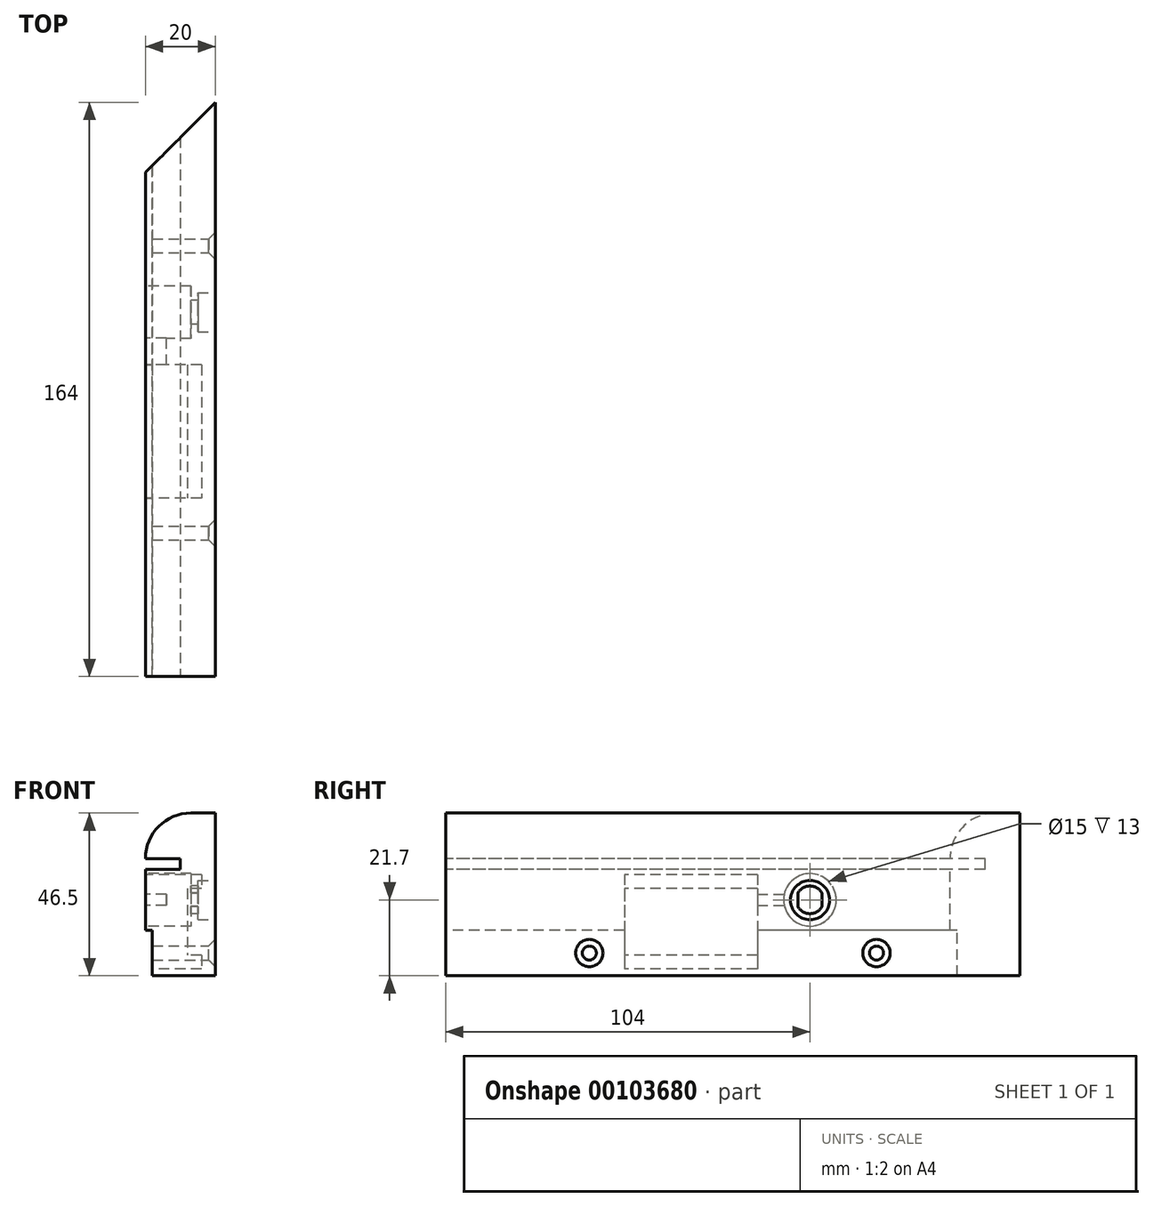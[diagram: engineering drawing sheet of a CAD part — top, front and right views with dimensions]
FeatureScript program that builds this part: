
annotation { "Feature Type Name" : "Feature", "Feature Type Description" : "" }
export const myFeature = defineFeature(function(context is Context, id is Id, definition is map)
    precondition{}
    {
        {
            var Q0;
            Q0=qCreatedBy(makeId("Front.planeOp"),FACE);
            var sketch = newSketch(context, id + "F0", { "sketchPlane" : qUnion([Q0])});
            skLineSegment(sketch, "E0.bottom", {"start": v(10, 23.25) * mm, "end": v(-10, 23.25) * mm});
            skLineSegment(sketch, "E0.top", {"start": v(10, -23.25) * mm, "end": v(-10, -23.25) * mm});
            skLineSegment(sketch, "E0.left", {"start": v(10, 23.25) * mm, "end": v(10, -23.25) * mm});
            skLineSegment(sketch, "E0.right", {"start": v(-10, 23.25) * mm, "end": v(-10, -23.25) * mm});
            skPoint(sketch, "E0.middle", {"position": v(0, 0) * mm});
            skSolve(sketch);
        }
        {
            var Q0;
            Q0=makeQuery(id+"F0.imprint","IMPRINT",FACE,{"disambiguationData":[TD([[makeQuery(id+"F0.imprint","IMPRINT",EDGE,{"derivedFrom":sQuery(id+"F0.wireOp",EDGE,"E0.bottom")}),1.0]])]});
            extrude(context, id + "F1", {"entities" : qUnion([Q0]), "depth" : 164 * mm});
        }
        {
            var Q0;
            Q0=makeQuery(id+"F1.opExtrude","SWEPT_FACE",FACE,{"disambiguationData":[OSD([sQuery(id+"F0.wireOp",EDGE,"E0.right")])]});
            var sketch = newSketch(context, id + "F2", { "sketchPlane" : qUnion([Q0])});
            skLineSegment(sketch, "E1.bottom", {"start": v(0, 10.25) * mm, "end": v(164, 10.25) * mm});
            skLineSegment(sketch, "E1.top", {"start": v(0, 7.15) * mm, "end": v(164, 7.15) * mm});
            skLineSegment(sketch, "E1.left", {"start": v(0, 10.25) * mm, "end": v(0, 7.15) * mm});
            skLineSegment(sketch, "E1.right", {"start": v(164, 10.25) * mm, "end": v(164, 7.15) * mm});
            skLineSegment(sketch, "E2.bottom", {"start": v(0, -23.25) * mm, "end": v(164, -23.25) * mm});
            skLineSegment(sketch, "E2.top", {"start": v(0, -10.25) * mm, "end": v(164, -10.25) * mm});
            skLineSegment(sketch, "E2.left", {"start": v(0, -23.25) * mm, "end": v(0, -10.25) * mm});
            skLineSegment(sketch, "E2.right", {"start": v(164, -23.25) * mm, "end": v(164, -10.25) * mm});
            skSolve(sketch);
        }
        {
            var Q0;
            Q0=makeQuery(id+"F2.imprint","IMPRINT",FACE,{"disambiguationData":[TD([[makeQuery(id+"F2.imprint","IMPRINT",EDGE,{"derivedFrom":sQuery(id+"F2.wireOp",EDGE,"E1.bottom")}),-1.0]])]});
            extrude(context, id + "F3", {"entities" : qUnion([Q0]), "operationType" : NewBodyOperationType.REMOVE, "oppositeDirection" : true, "depth" : 10 * mm});
        }
        {
            var Q0;
            {var subQ0=sQuery(id+"F0.wireOp",EDGE,"E0.right");var subQ2=sQuery(id+"F0.wireOp",EDGE,"E0.top");Q0=makeQuery(id+"F3.boolean.opBoolean","SPLIT",FACE,{"disambiguationData":[TD([makeQuery(id+"F1.opExtrude","SWEPT_FACE",FACE,{"disambiguationData":[OSD([subQ2])]})])],"derivedFrom":makeQuery(id+"F1.opExtrude","SWEPT_FACE",FACE,{"disambiguationData":[OSD([subQ0])]})});}
            var sketch = newSketch(context, id + "F4", { "sketchPlane" : qUnion([Q0])});
            skLineSegment(sketch, "E3.bottom", {"start": v(0, -23.25) * mm, "end": v(164, -23.25) * mm});
            skLineSegment(sketch, "E3.top", {"start": v(0, -10.25) * mm, "end": v(164, -10.25) * mm});
            skLineSegment(sketch, "E3.left", {"start": v(0, -23.25) * mm, "end": v(0, -10.25) * mm});
            skLineSegment(sketch, "E3.right", {"start": v(164, -23.25) * mm, "end": v(164, -10.25) * mm});
            skSolve(sketch);
        }
        {
            var Q0;
            Q0=makeQuery(id+"F4.imprint","IMPRINT",FACE,{"disambiguationData":[TD([[makeQuery(id+"F4.imprint","IMPRINT",EDGE,{"derivedFrom":sQuery(id+"F4.wireOp",EDGE,"E3.bottom")}),-1.0]])]});
            extrude(context, id + "F5", {"entities" : qUnion([Q0]), "operationType" : NewBodyOperationType.REMOVE, "oppositeDirection" : true, "depth" : 2 * mm});
        }
        {
            var Q0;
            Q0=makeQuery(id+"F1.opExtrude","SWEPT_FACE",FACE,{"disambiguationData":[OSD([sQuery(id+"F0.wireOp",EDGE,"E0.bottom")])]});
            var sketch = newSketch(context, id + "F6", { "sketchPlane" : qUnion([Q0])});
            skLineSegment(sketch, "E4.bottom", {"start": v(10, 0) * mm, "end": v(-10, 0) * mm, "construction": true});
            skLineSegment(sketch, "E4.top", {"start": v(10, -20) * mm, "end": v(-10, -20) * mm, "construction": true});
            skLineSegment(sketch, "E4.left", {"start": v(10, 0) * mm, "end": v(10, -20) * mm, "construction": true});
            skLineSegment(sketch, "E4.right", {"start": v(-10, 0) * mm, "end": v(-10, -20) * mm, "construction": true});
            skLineSegment(sketch, "E5", {"start": v(-10, -20) * mm, "end": v(10, 0) * mm});
            skLineSegment(sketch, "E6", {"start": v(-10, -20) * mm, "end": v(-10, 0) * mm});
            skLineSegment(sketch, "E7", {"start": v(-10, 0) * mm, "end": v(10, 0) * mm});
            skSolve(sketch);
        }
        {
            var Q0;
            Q0=makeQuery(id+"F6.imprint","IMPRINT",FACE,{"disambiguationData":[TD([[makeQuery(id+"F6.imprint","IMPRINT",EDGE,{"derivedFrom":sQuery(id+"F6.wireOp",EDGE,"E5")}),1.0]])]});
            var Q1;
            Q1=makeQuery(id+"F1.opExtrude","SWEPT_FACE",FACE,{"disambiguationData":[OSD([sQuery(id+"F0.wireOp",EDGE,"E0.top")])]});
            extrude(context, id + "F7", {"entities" : qUnion([Q0]), "operationType" : NewBodyOperationType.REMOVE, "endBound" : BoundingType.UP_TO_SURFACE, "oppositeDirection" : true, "endBoundEntityFace" : qUnion([Q1]), "depth" : 25 * mm});
        }
        {
            var Q0;
            Q0=makeQuery(id+"F1.opExtrude","SWEPT_EDGE",EDGE,{"disambiguationData":[OSD([sQuery(id+"F0.wireOp",EDGE,"E0.bottom"),sQuery(id+"F0.wireOp",EDGE,"E0.right")])]});
            fillet(context, id + "F8", {"entities" : qUnion([Q0]), "radius" : 13 * mm, "tangentPropagation" : true, "allowEdgeOverflow" : false});
        }
        {
            var Q0;
            Q0=makeQuery(id+"F1.opExtrude","SWEPT_FACE",FACE,{"disambiguationData":[OSD([sQuery(id+"F0.wireOp",EDGE,"E0.left")])]});
            var sketch = newSketch(context, id + "F9", { "sketchPlane" : qUnion([Q0])});
            skLineSegment(sketch, "E8", {"start": v(-82, 23.25) * mm, "end": v(-82, -23.25) * mm, "construction": true});
            skLineSegment(sketch, "E9", {"start": v(-164, -16.75) * mm, "end": v(-82, -16.75) * mm, "construction": true});
            skLineSegment(sketch, "E10", {"start": v(-82, -16.75) * mm, "end": v(0, -16.75) * mm, "construction": true});
            skPoint(sketch, "E11", {"position": v(-123, -16.75) * mm});
            skPoint(sketch, "E12", {"position": v(-41, -16.75) * mm});
            skSolve(sketch);
        }
        {
            var Q0;
            Q0=sQuery(id+"F9.wireOp",VERTEX,"E11");
            var Q1;
            Q1=sQuery(id+"F9.wireOp",VERTEX,"E12");
            var Q2;
            Q2=makeQuery(id+"F1.opExtrude","SWEPT_BODY",BODY,{"disambiguationData":[OSD([sQuery(id+"F0.wireOp",EDGE,"E0.bottom"),sQuery(id+"F0.wireOp",EDGE,"E0.top"),sQuery(id+"F0.wireOp",EDGE,"E0.left"),sQuery(id+"F0.wireOp",EDGE,"E0.right")])]});
            hole(context, id + "F10", {"style" : HoleStyle.C_SINK, "endStyle" : HoleEndStyle.BLIND, "holeDiameter" : 4 * mm, "cSinkDiameter" : 7.8 * mm, "cSinkAngle" : 90 * degree, "holeDepth" : 20 * mm, "tappedDepth" : 12 * mm, "tapClearance" : 3, "locations" : qUnion([Q0, Q1]), "scope" : qUnion([Q2])});
        }
        {
            var Q0;
            {var subQ0=sQuery(id+"F0.wireOp",EDGE,"E0.right");var subQ2=sQuery(id+"F0.wireOp",EDGE,"E0.top");Q0=makeQuery(id+"F3.boolean.opBoolean","SPLIT",FACE,{"disambiguationData":[TD([makeQuery(id+"F1.opExtrude","SWEPT_FACE",FACE,{"disambiguationData":[OSD([subQ2])]})])],"derivedFrom":makeQuery(id+"F1.opExtrude","SWEPT_FACE",FACE,{"disambiguationData":[OSD([subQ0])]})});}
            var sketch = newSketch(context, id + "F11", { "sketchPlane" : qUnion([Q0])});
            skLineSegment(sketch, "E13", {"start": v(20, -1.55) * mm, "end": v(164, -1.55) * mm, "construction": true});
            skArc(sketch, "E14", {"start": v(63.4, 0.45) * mm, "mid": v(59.9, 2.4) * mm, "end": v(56.5, 0.3) * mm});
            skLineSegment(sketch, "E15.left", {"start": v(56.5, 0.3) * mm, "end": v(56.5, -3.4) * mm});
            skLineSegment(sketch, "E15.right", {"start": v(63.4, 0.45) * mm, "end": v(63.4, -3.55) * mm});
            skArc(sketch, "E16.trimOffspring", {"start": v(56.5, -3.4) * mm, "mid": v(59.9, -5.5) * mm, "end": v(63.4, -3.55) * mm});
            skSolve(sketch);
        }
        {
            var Q0;
            Q0=makeQuery(id+"F11.imprint","IMPRINT",FACE,{"disambiguationData":[TD([[makeQuery(id+"F11.imprint","IMPRINT",EDGE,{"derivedFrom":sQuery(id+"F11.wireOp",EDGE,"E14")}),1.0]])]});
            var Q1;
            Q1=makeQuery(id+"F1.opExtrude","SWEPT_FACE",FACE,{"disambiguationData":[OSD([sQuery(id+"F0.wireOp",EDGE,"E0.left")])]});
            extrude(context, id + "F12", {"entities" : qUnion([Q0]), "operationType" : NewBodyOperationType.REMOVE, "endBound" : BoundingType.UP_TO_SURFACE, "oppositeDirection" : true, "endBoundEntityFace" : qUnion([Q1]), "depth" : 25 * mm});
        }
        {
            var Q0;
            {var subQ0=sQuery(id+"F0.wireOp",EDGE,"E0.right");var subQ2=sQuery(id+"F0.wireOp",EDGE,"E0.top");Q0=makeQuery(id+"F3.boolean.opBoolean","SPLIT",FACE,{"disambiguationData":[TD([makeQuery(id+"F1.opExtrude","SWEPT_FACE",FACE,{"disambiguationData":[OSD([subQ2])]})])],"derivedFrom":makeQuery(id+"F1.opExtrude","SWEPT_FACE",FACE,{"disambiguationData":[OSD([subQ0])]})});}
            var sketch = newSketch(context, id + "F13", { "sketchPlane" : qUnion([Q0])});
            skLineSegment(sketch, "E17", {"start": v(20, -1.55) * mm, "end": v(164, -1.55) * mm, "construction": true});
            skCircle(sketch, "E18", {"center": v(60, -1.55) * mm, "radius": 7.5 * mm});
            skSolve(sketch);
        }
        {
            var Q0;
            Q0=makeQuery(id+"F13.imprint","IMPRINT",FACE,{"disambiguationData":[TD([[makeQuery(id+"F13.imprint","IMPRINT",EDGE,{"derivedFrom":sQuery(id+"F13.wireOp",EDGE,"E18")}),1.0]])]});
            extrude(context, id + "F14", {"entities" : qUnion([Q0]), "operationType" : NewBodyOperationType.REMOVE, "oppositeDirection" : true, "depth" : 13 * mm});
        }
        {
            var Q0;
            Q0=makeQuery(id+"F1.opExtrude","SWEPT_FACE",FACE,{"disambiguationData":[OSD([sQuery(id+"F0.wireOp",EDGE,"E0.left")])]});
            var sketch = newSketch(context, id + "F15", { "sketchPlane" : qUnion([Q0])});
            skLineSegment(sketch, "E19", {"start": v(-63.4, 0.45) * mm, "end": v(-56.5, -3.4) * mm, "construction": true});
            skLineSegment(sketch, "E20", {"start": v(-56.5, 0.3) * mm, "end": v(-63.4, -3.55) * mm, "construction": true});
            skPoint(sketch, "E21", {"position": v(-59.96, -1.63) * mm});
            skCircle(sketch, "E22", {"center": v(-59.96, -1.63) * mm, "radius": 5.6 * mm});
            skSolve(sketch);
        }
        {
            var Q0;
            Q0=makeQuery(id+"F15.imprint","IMPRINT",FACE,{"disambiguationData":[TD([[makeQuery(id+"F15.imprint","IMPRINT",EDGE,{"derivedFrom":sQuery(id+"F15.wireOp",EDGE,"E22")}),1.0]])]});
            var Q1;
            Q1=sQuery(id+"F15.wireOp",EDGE,"E22");
            extrude(context, id + "F16", {"entities" : qUnion([Q0]), "operationType" : NewBodyOperationType.REMOVE, "surfaceEntities" : qUnion([Q1]), "oppositeDirection" : true, "depth" : 5 * mm});
        }
        {
            var Q0;
            {var subQ0=sQuery(id+"F0.wireOp",EDGE,"E0.right");var subQ2=sQuery(id+"F0.wireOp",EDGE,"E0.top");Q0=makeQuery(id+"F3.boolean.opBoolean","SPLIT",FACE,{"disambiguationData":[TD([makeQuery(id+"F1.opExtrude","SWEPT_FACE",FACE,{"disambiguationData":[OSD([subQ2])]})])],"derivedFrom":makeQuery(id+"F1.opExtrude","SWEPT_FACE",FACE,{"disambiguationData":[OSD([subQ0])]})});}
            var sketch = newSketch(context, id + "F17", { "sketchPlane" : qUnion([Q0])});
            skLineSegment(sketch, "E23.bottom", {"start": v(75, 5.65) * mm, "end": v(113, 5.65) * mm});
            skLineSegment(sketch, "E23.top", {"start": v(75, -21.35) * mm, "end": v(113, -21.35) * mm});
            skLineSegment(sketch, "E23.left", {"start": v(75, 5.65) * mm, "end": v(75, -21.35) * mm});
            skLineSegment(sketch, "E23.right", {"start": v(113, 5.65) * mm, "end": v(113, -21.35) * mm});
            skSolve(sketch);
        }
        {
            var Q0;
            {var subQ0=sQuery(id+"F17.wireOp",EDGE,"E23.bottom");Q0=makeQuery(id+"F17.imprint","IMPRINT",FACE,{"disambiguationData":[TD([[makeQuery(id+"F17.imprint","IMPRINT",EDGE,{"derivedFrom":subQ0}),-1.0]])]});}
            var Q1;
            {var subQ0=sQuery(id+"F17.wireOp",EDGE,"E23.top");Q1=makeQuery(id+"F17.imprint","IMPRINT",FACE,{"disambiguationData":[TD([[makeQuery(id+"F17.imprint","IMPRINT",EDGE,{"derivedFrom":subQ0}),1.0]])]});}
            extrude(context, id + "F18", {"entities" : qUnion([Q0, Q1]), "operationType" : NewBodyOperationType.REMOVE, "oppositeDirection" : true, "depth" : 12 * mm});
        }
        {
            var Q0;
            {var subQ0=sQuery(id+"F0.wireOp",EDGE,"E0.right");var subQ2=sQuery(id+"F0.wireOp",EDGE,"E0.top");Q0=makeQuery(id+"F3.boolean.opBoolean","SPLIT",FACE,{"disambiguationData":[TD([makeQuery(id+"F1.opExtrude","SWEPT_FACE",FACE,{"disambiguationData":[OSD([subQ2])]})])],"derivedFrom":makeQuery(id+"F1.opExtrude","SWEPT_FACE",FACE,{"disambiguationData":[OSD([subQ0])]})});}
            var sketch = newSketch(context, id + "F19", { "sketchPlane" : qUnion([Q0])});
            skLineSegment(sketch, "E24.bottom", {"start": v(75, 0) * mm, "end": v(67.34, 0) * mm});
            skLineSegment(sketch, "E24.top", {"start": v(75, -3.1) * mm, "end": v(67.34, -3.1) * mm});
            skLineSegment(sketch, "E24.left", {"start": v(75, 0) * mm, "end": v(75, -3.1) * mm});
            skLineSegment(sketch, "E24.right", {"start": v(67.34, 0) * mm, "end": v(67.34, -3.1) * mm});
            skSolve(sketch);
        }
        {
            var Q0;
            {var subQ0=sQuery(id+"F19.wireOp",EDGE,"E24.bottom");Q0=makeQuery(id+"F19.imprint","IMPRINT",FACE,{"disambiguationData":[TD([[makeQuery(id+"F19.imprint","IMPRINT",EDGE,{"derivedFrom":subQ0}),1.0]])]});}
            extrude(context, id + "F20", {"entities" : qUnion([Q0]), "operationType" : NewBodyOperationType.REMOVE, "oppositeDirection" : true, "depth" : 6 * mm});
        }
        {
            var Q0;
            Q0=makeQuery(id+"F18.boolean.opBoolean","COPY",FACE,{"derivedFrom":makeQuery(id+"F18.opExtrude","CAP_FACE",FACE,{"disambiguationData":[OSD([sQuery(id+"F17.wireOp",EDGE,"E23.bottom"),sQuery(id+"F17.wireOp",EDGE,"E23.top"),sQuery(id+"F17.wireOp",EDGE,"E23.left"),sQuery(id+"F17.wireOp",EDGE,"E23.right")])],"isStart":false})});
            var sketch = newSketch(context, id + "F21", { "sketchPlane" : qUnion([Q0])});
            skLineSegment(sketch, "E25.bottom", {"start": v(75, 5.65) * mm, "end": v(113, 5.65) * mm});
            skLineSegment(sketch, "E25.top", {"start": v(75, 1.65) * mm, "end": v(113, 1.65) * mm});
            skLineSegment(sketch, "E25.left", {"start": v(75, 5.65) * mm, "end": v(75, 1.65) * mm});
            skLineSegment(sketch, "E25.right", {"start": v(113, 5.65) * mm, "end": v(113, 1.65) * mm});
            skSolve(sketch);
        }
        {
            var Q0;
            Q0=makeQuery(id+"F21.imprint","IMPRINT",FACE,{"disambiguationData":[TD([[makeQuery(id+"F21.imprint","IMPRINT",EDGE,{"derivedFrom":sQuery(id+"F21.wireOp",EDGE,"E25.bottom")}),-1.0]])]});
            extrude(context, id + "F22", {"entities" : qUnion([Q0]), "operationType" : NewBodyOperationType.REMOVE, "oppositeDirection" : true, "depth" : 4 * mm});
        }
        {
            var Q0;
            Q0=makeQuery(id+"F18.boolean.opBoolean","COPY",FACE,{"derivedFrom":makeQuery(id+"F18.opExtrude","CAP_FACE",FACE,{"disambiguationData":[OSD([sQuery(id+"F17.wireOp",EDGE,"E23.bottom"),sQuery(id+"F17.wireOp",EDGE,"E23.top"),sQuery(id+"F17.wireOp",EDGE,"E23.left"),sQuery(id+"F17.wireOp",EDGE,"E23.right")])],"isStart":false})});
            var sketch = newSketch(context, id + "F23", { "sketchPlane" : qUnion([Q0])});
            skLineSegment(sketch, "E26.bottom", {"start": v(75, -21.35) * mm, "end": v(113, -21.35) * mm});
            skLineSegment(sketch, "E26.top", {"start": v(75, -17.35) * mm, "end": v(113, -17.35) * mm});
            skLineSegment(sketch, "E26.left", {"start": v(75, -21.35) * mm, "end": v(75, -17.35) * mm});
            skLineSegment(sketch, "E26.right", {"start": v(113, -21.35) * mm, "end": v(113, -17.35) * mm});
            skSolve(sketch);
        }
        {
            var Q0;
            Q0=makeQuery(id+"F23.imprint","IMPRINT",FACE,{"disambiguationData":[TD([[makeQuery(id+"F23.imprint","IMPRINT",EDGE,{"derivedFrom":sQuery(id+"F23.wireOp",EDGE,"E26.bottom")}),1.0]])]});
            extrude(context, id + "F24", {"entities" : qUnion([Q0]), "operationType" : NewBodyOperationType.REMOVE, "oppositeDirection" : true, "depth" : 4 * mm});
        }
    });
